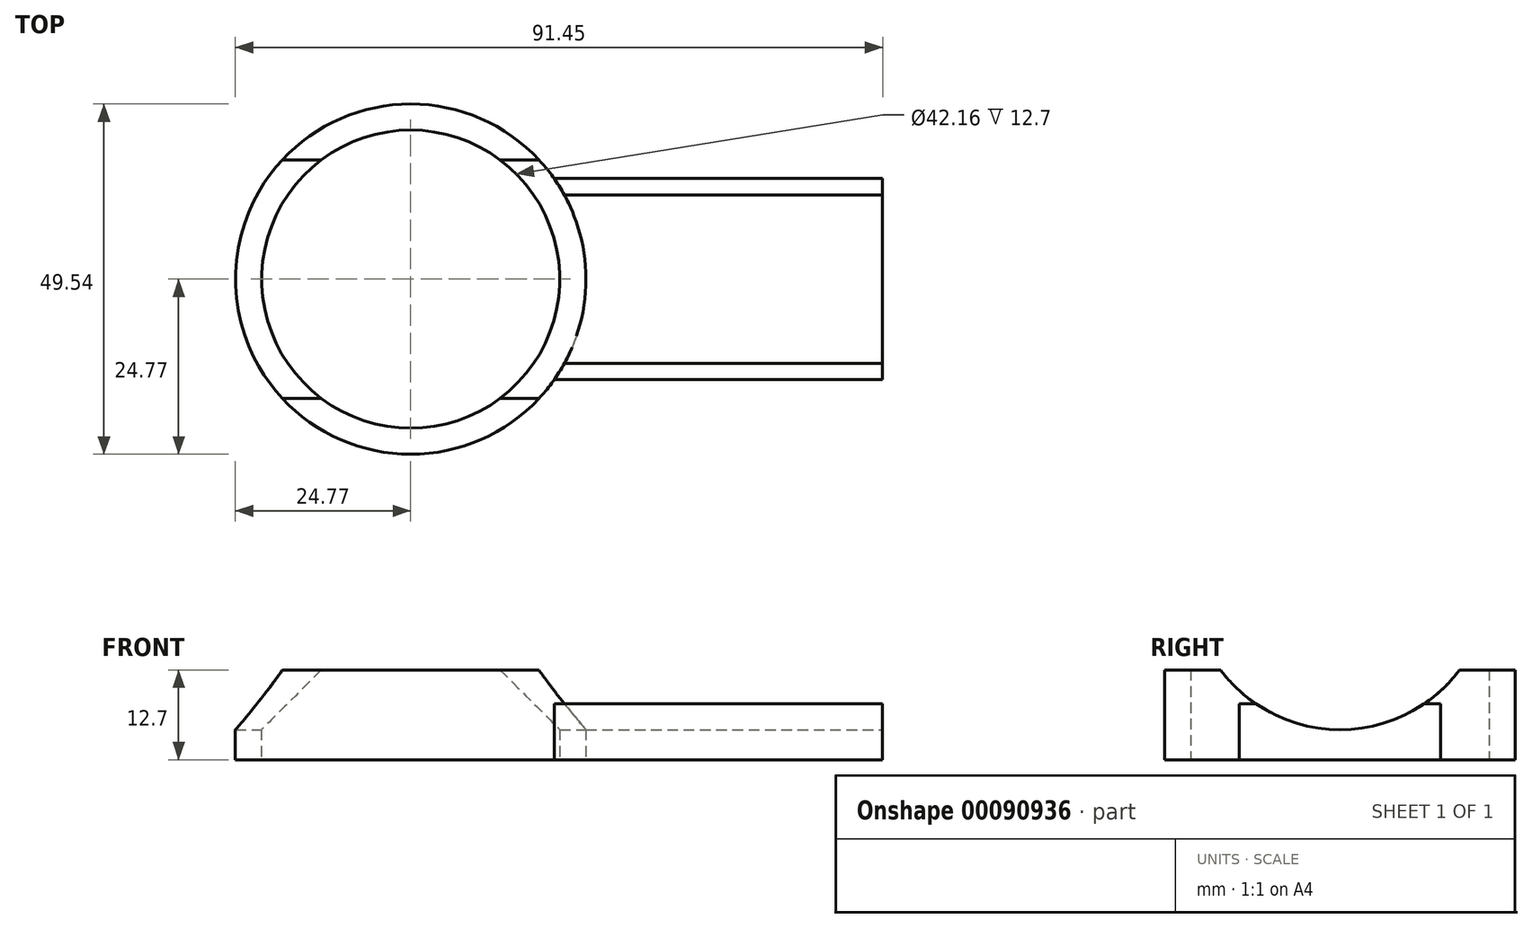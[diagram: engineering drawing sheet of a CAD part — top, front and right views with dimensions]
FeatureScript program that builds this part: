
annotation { "Feature Type Name" : "Feature", "Feature Type Description" : "" }
export const myFeature = defineFeature(function(context is Context, id is Id, definition is map)
    precondition{}
    {
        {
            var Q0;
            Q0=qCreatedBy(makeId("Top.planeOp"),FACE);
            var sketch = newSketch(context, id + "F0", { "sketchPlane" : qUnion([Q0])});
            skCircle(sketch, "E0", {"center": v(0, 0) * mm, "radius": 21.08 * mm});
            skCircle(sketch, "E1", {"center": v(0, 0) * mm, "radius": 24.77 * mm});
            skLineSegment(sketch, "E2.bottom", {"start": v(0, 14.22) * mm, "end": v(66.68, 14.22) * mm});
            skLineSegment(sketch, "E2.top", {"start": v(0, -14.22) * mm, "end": v(66.68, -14.22) * mm});
            skLineSegment(sketch, "E2.left", {"start": v(0, 14.22) * mm, "end": v(0, -14.22) * mm});
            skLineSegment(sketch, "E2.right", {"start": v(66.68, 14.22) * mm, "end": v(66.68, -14.22) * mm});
            skLineSegment(sketch, "E3", {"start": v(0, 0) * mm, "end": v(68.85, 0) * mm, "construction": true});
            skSolve(sketch);
        }
        {
            var Q0;
            {var subQ0=sQuery(id+"F0.wireOp",EDGE,"E2.bottom");var subQ1=sQuery(id+"F0.wireOp",EDGE,"E0");var subQ2=makeQuery(id+"F0.imprint","INTERSECT",VERTEX,{"derivedFrom":[subQ1,subQ0]});Q0=makeQuery(id+"F0.imprint","IMPRINT",FACE,{"disambiguationData":[TD([[makeQuery(id+"F0.imprint","IMPRINT",EDGE,{"disambiguationData":[TD([[subQ2,-1.0]])],"derivedFrom":subQ1}),-1.0]])]});}
            var Q1;
            {var subQ0=sQuery(id+"F0.wireOp",EDGE,"E2.bottom");var subQ1=sQuery(id+"F0.wireOp",EDGE,"E0");var subQ2=makeQuery(id+"F0.imprint","INTERSECT",VERTEX,{"derivedFrom":[subQ1,subQ0]});Q1=makeQuery(id+"F0.imprint","IMPRINT",FACE,{"disambiguationData":[TD([[makeQuery(id+"F0.imprint","IMPRINT",EDGE,{"disambiguationData":[TD([[subQ2,1.0]])],"derivedFrom":subQ1}),-1.0]])]});}
            extrude(context, id + "F1", {"entities" : qUnion([Q0, Q1]), "depth" : 12.7 * mm});
        }
        {
            var Q0;
            {var subQ5=sQuery(id+"F0.wireOp",EDGE,"E2.right");Q0=makeQuery(id+"F0.imprint","IMPRINT",FACE,{"disambiguationData":[TD([[makeQuery(id+"F0.imprint","IMPRINT",EDGE,{"derivedFrom":subQ5}),-1.0]])]});}
            extrude(context, id + "F2", {"entities" : qUnion([Q0]), "depth" : 7.92 * mm});
        }
        {
            var Q0;
            Q0=makeQuery(id+"F2.opExtrude","SWEPT_FACE",FACE,{"disambiguationData":[OSD([sQuery(id+"F0.wireOp",EDGE,"E2.right")])]});
            var sketch = newSketch(context, id + "F3", { "sketchPlane" : qUnion([Q0])});
            skCircle(sketch, "E4", {"center": v(0, 25.34) * mm, "radius": 21.08 * mm});
            skSolve(sketch);
        }
        {
            var Q0;
            {var subQ0=sQuery(id+"F3.wireOp",EDGE,"E4");var subQ1=makeQuery(id+"F2.opExtrude","CAP_EDGE",EDGE,{"disambiguationData":[OSD([sQuery(id+"F0.wireOp",EDGE,"E2.right")])],"isStart":false});var subQ2=makeQuery(id+"F3.imprint","INTERSECT",VERTEX,{"disambiguationData":[OD(0.0)],"derivedFrom":[subQ1,subQ0]});Q0=makeQuery(id+"F3.imprint","IMPRINT",FACE,{"disambiguationData":[TD([[makeQuery(id+"F3.imprint","IMPRINT",EDGE,{"disambiguationData":[TD([[subQ2,-1.0]])],"derivedFrom":subQ0}),1.0]])]});}
            var Q1;
            {var subQ0=sQuery(id+"F3.wireOp",EDGE,"E4");var subQ1=makeQuery(id+"F2.opExtrude","CAP_EDGE",EDGE,{"disambiguationData":[OSD([sQuery(id+"F0.wireOp",EDGE,"E2.right")])],"isStart":false});var subQ2=makeQuery(id+"F3.imprint","INTERSECT",VERTEX,{"disambiguationData":[OD(0.0)],"derivedFrom":[subQ1,subQ0]});Q1=makeQuery(id+"F3.imprint","IMPRINT",FACE,{"disambiguationData":[TD([[makeQuery(id+"F3.imprint","IMPRINT",EDGE,{"disambiguationData":[TD([[subQ2,1.0]])],"derivedFrom":subQ0}),1.0]])]});}
            extrude(context, id + "F4", {"entities" : qUnion([Q0, Q1]), "operationType" : NewBodyOperationType.REMOVE, "endBound" : BoundingType.THROUGH_ALL, "oppositeDirection" : true, "depth" : 25.4 * mm});
        }
    });
